# Revit family: FU_Table_Sandler_594-XT
name_source: partatom
category: Furniture
units: mm (PartAtom-declared; Revit-internal decimal feet)

## family parameters
Always vertical = Yes
Cut with Voids When Loaded = No
OmniClass Number = 23.40.20.00
OmniClass Title = General Furniture and Specialties
Room Calculation Point = No
Shared = No
Work Plane-Based = No

## types (3) — shared parameters
Depth = 425 mm  [stored 1.39436 ft]
Description = Table base in stainless steel.
Height = 720 mm  [stored 2.3622 ft]
Manufacturer = Sandler
Model = 594 XT
Top Elevation = 720 mm  [stored 2.3622 ft]
URL = https://www.sandlerseating.com
Width = 425 mm  [stored 1.39436 ft]
zero-valued in all types: Default Elevation

## per-type parameters (varying)
| type | Top Type |
| 594 XT - 24" Round Top (60cm) | FU_TableTops_MT Rnd : 24" Round (60cm) |
| 594 XT - 28" Round Top (70cm) | FU_TableTops_MT Rnd : 28" Round (70cm) |
| 594 XT - 24" Square Top (60cm) | FU_TableTops_MT Sqr : 24" Square (60cm) |

note: [stored X ft] marks values corroborated as IEEE doubles in the binary element streams (Revit-internal decimal feet)

## geometry (parser evidence)
native form markers: Sweep x11
no freeform markers — native parametric forms only
